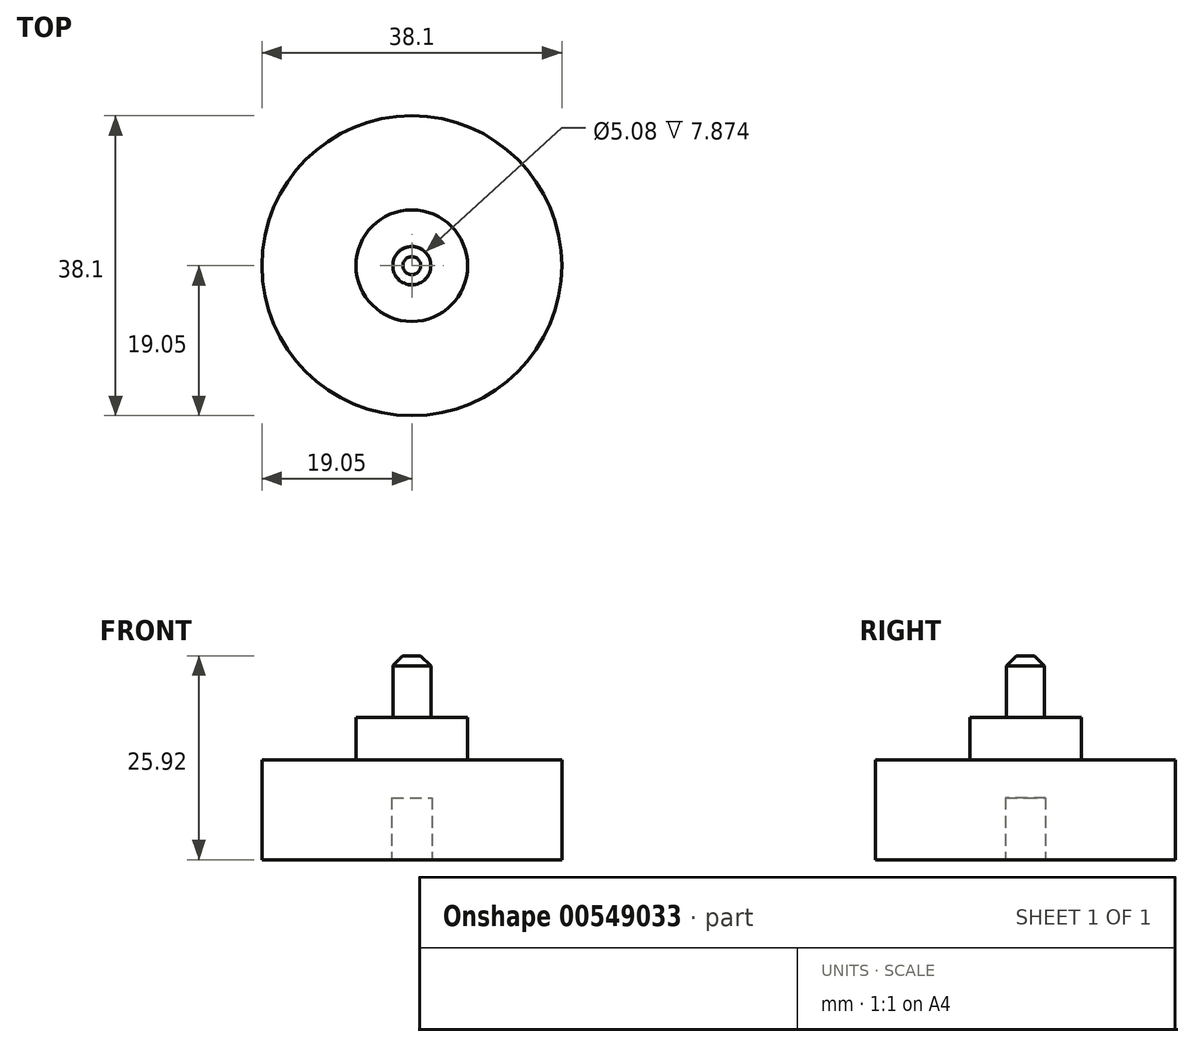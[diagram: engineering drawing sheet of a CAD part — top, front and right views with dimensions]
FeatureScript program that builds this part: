
annotation { "Feature Type Name" : "Feature", "Feature Type Description" : "" }
export const myFeature = defineFeature(function(context is Context, id is Id, definition is map)
    precondition{}
    {
        {
            var Q0;
            Q0=qCreatedBy(makeId("Front.planeOp"),FACE);
            var sketch = newSketch(context, id + "F0", { "sketchPlane" : qUnion([Q0])});
            skLineSegment(sketch, "E0", {"start": v(0, 0) * mm, "end": v(19.05, 0) * mm});
            skLineSegment(sketch, "E1", {"start": v(19.05, 0) * mm, "end": v(19.05, 12.7) * mm});
            skLineSegment(sketch, "E2", {"start": v(19.05, 12.7) * mm, "end": v(7.09, 12.7) * mm});
            skLineSegment(sketch, "E3", {"start": v(0, 0) * mm, "end": v(2.54, 0) * mm});
            skLineSegment(sketch, "E4", {"start": v(2.54, 0) * mm, "end": v(2.54, 7.87) * mm});
            skLineSegment(sketch, "E5", {"start": v(2.54, 7.87) * mm, "end": v(0, 7.87) * mm});
            skLineSegment(sketch, "E6", {"start": v(2.41, 18.07) * mm, "end": v(7.09, 18.07) * mm});
            skLineSegment(sketch, "E7", {"start": v(7.09, 18.07) * mm, "end": v(7.09, 12.7) * mm});
            skPoint(sketch, "E8.start.orphan", {"position": v(0, 12.7) * mm});
            skLineSegment(sketch, "E9", {"start": v(0, 25.92) * mm, "end": v(2.41, 25.92) * mm});
            skLineSegment(sketch, "E10", {"start": v(2.41, 25.92) * mm, "end": v(2.41, 18.07) * mm});
            skPoint(sketch, "E11.orphan", {"position": v(2.41, 12.7) * mm});
            skLineSegment(sketch, "E12", {"start": v(0, 7.87) * mm, "end": v(0, 25.92) * mm});
            skSolve(sketch);
        }
        {
            var Q0;
            Q0 = qSketchRegion(id + "F0", true);
            var Q1;
            Q1=sQuery(id+"F0.wireOp",EDGE,"E12");
            revolve(context, id + "F1", {"entities" : qUnion([Q0]), "axis" : qUnion([Q1]), "revolveType" : RevolveType.FULL});
        }
        {
            var Q0;
            Q0=makeQuery(id+"F1.opRevolve","SWEPT_EDGE",EDGE,{"disambiguationData":[OSD([sQuery(id+"F0.wireOp",EDGE,"E9"),sQuery(id+"F0.wireOp",EDGE,"E10")])]});
            chamfer(context, id + "F2", {"entities" : qUnion([Q0]), "width" : 1.27 * mm, "tangentPropagation" : true});
        }
    });
